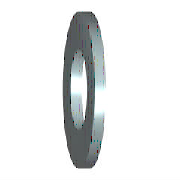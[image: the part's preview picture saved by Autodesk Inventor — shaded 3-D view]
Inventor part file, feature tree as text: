
AUTODESK INVENTOR PART (.ipt)
format: ipt  version: 2014 SP2 (Build 180246200, 246)  size: 106,496 bytes
history: native  units: mm (DEFAULTED — no unit token found)
features: extrude x1, other x1, plane x1, sketch x1
ambient origin geometry x7: Origin, YZ Plane, XY Plane, X Axis, Y Axis, Z Axis, Center Point
bodies: Solid1 (feature_tree)
feature tree (4):
  extrude  "Bryła"  Depth=6.4mm
  other  "Work Axis1"
  plane  "Work Plane1"
  sketch  "Szkic"
